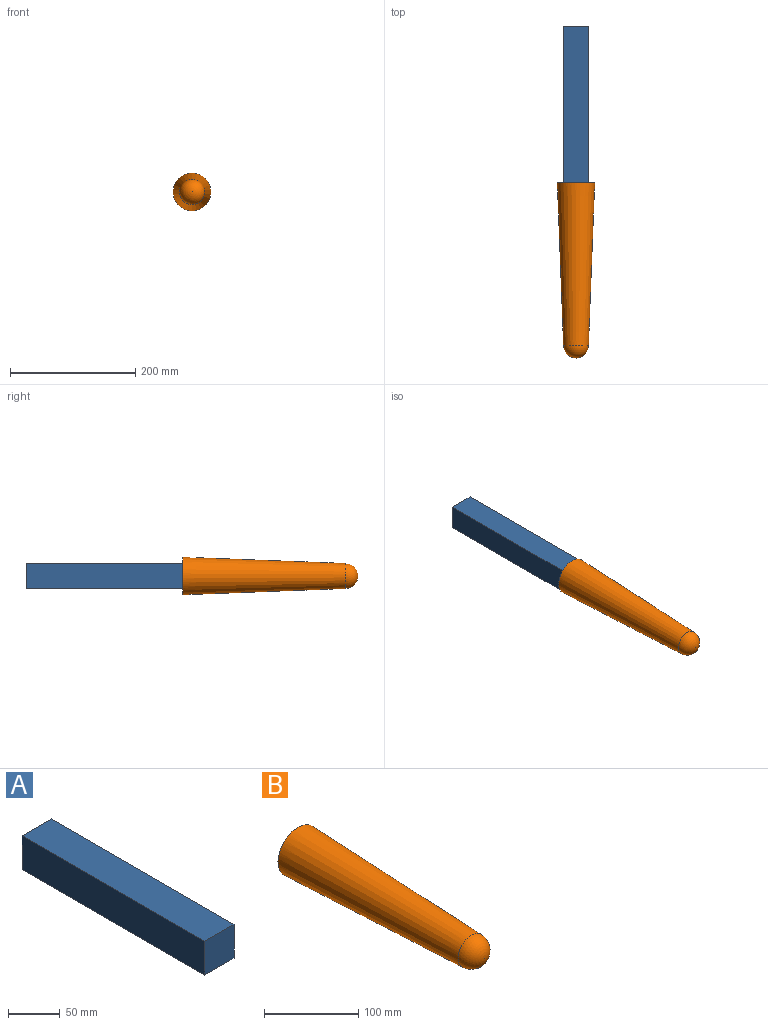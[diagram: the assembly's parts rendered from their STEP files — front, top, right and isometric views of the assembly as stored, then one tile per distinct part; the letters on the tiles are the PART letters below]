
ASSEMBLY  parts=2 mates=1
PART A: 6 faces, bbox 40x250x40 mm
  f0: plane 250x40mm, normal (0,0,1), area 10000mm2, adj f1,f3,f4,f5
  f1: plane 40x40mm, normal (0,-1,0), area 1600mm2, adj f0,f2,f4,f5
  f2: plane 250x40mm, normal (0,0,-1), area 10000mm2, adj f1,f3,f4,f5
  f3: plane 40x40mm, normal (0,1,0), area 1600mm2, adj f0,f2,f4,f5
  f4: plane 250x40mm, normal (1,0,0), area 10000mm2, adj f0,f1,f2,f3
  f5: plane 250x40mm, normal (-1,0,0), area 10000mm2, adj f0,f1,f2,f3
PART B: 3 faces, bbox 60x280x60 mm
  f0: sphere r=20.01mm, area 2450.8mm2, adj f2
  f1: plane 60x60mm, normal (0,1,0), area 2827.4mm2, adj f2
  f2: cone r=20mm half-angle=2.2deg, axis (0,1,0), area 40950mm2, adj f0,f1
PLACE A t=(-131.33,106.67,-123.75)mm
PLACE B t=(-131.33,-155.98,-123.75)mm
MATE fastened A.f1 <-> B.f2  axis (0,-1,0) through (-131.33,-18.33,-123.75)mm
